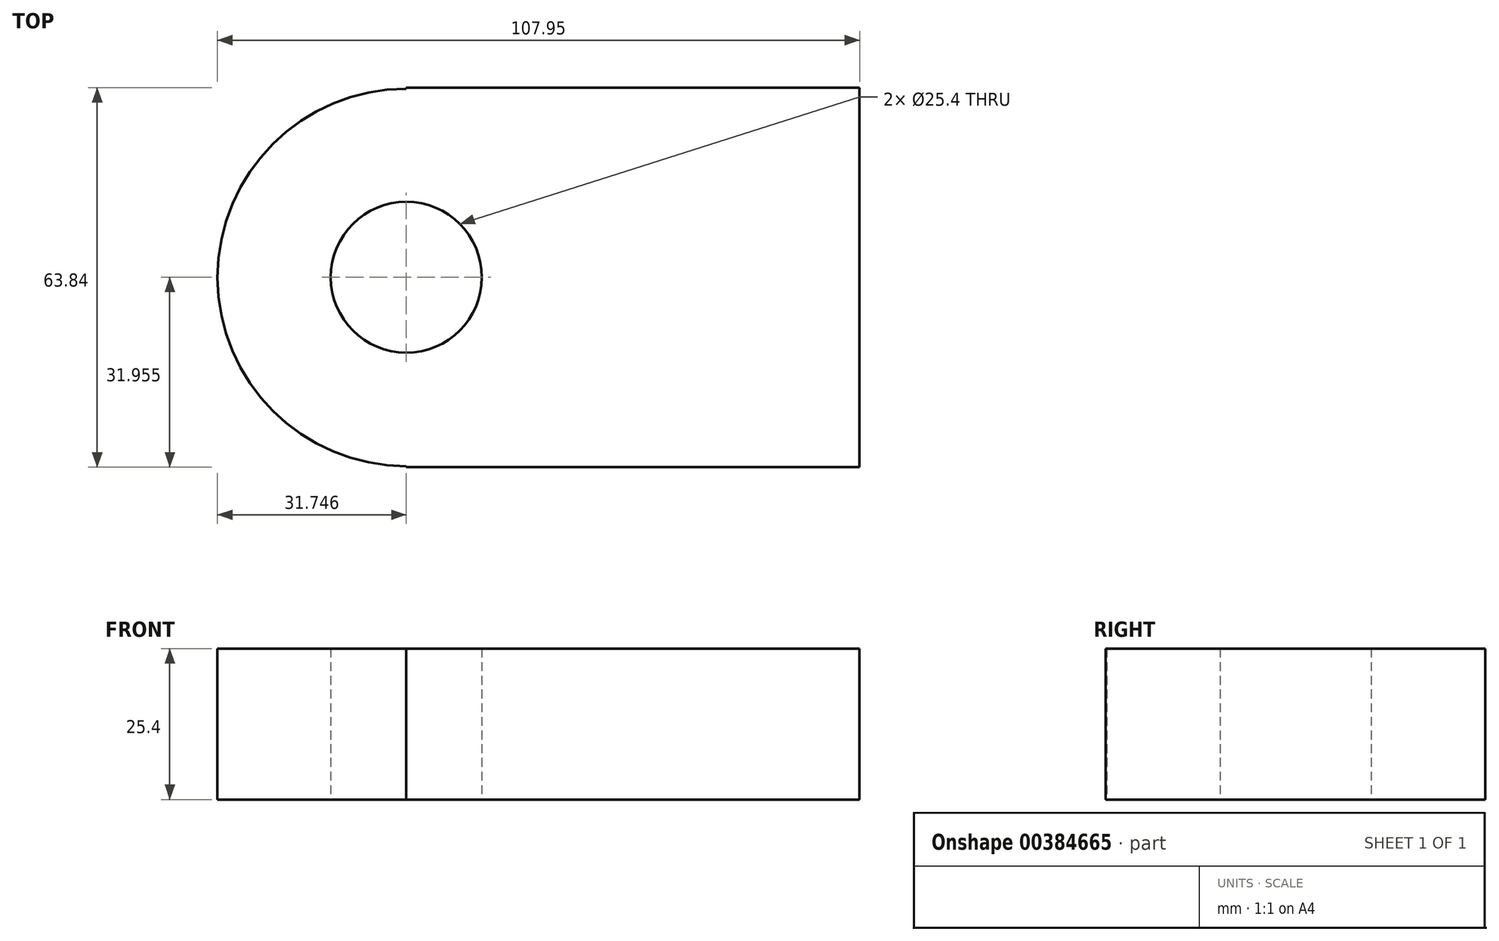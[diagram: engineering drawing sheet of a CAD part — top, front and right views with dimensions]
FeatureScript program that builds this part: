
annotation { "Feature Type Name" : "Feature", "Feature Type Description" : "" }
export const myFeature = defineFeature(function(context is Context, id is Id, definition is map)
    precondition{}
    {
        {
            var Q0;
            Q0=qCreatedBy(makeId("Top.planeOp"),FACE);
            var sketch = newSketch(context, id + "F0", { "sketchPlane" : qUnion([Q0])});
            skLineSegment(sketch, "E0.bottom", {"start": v(-38.22, -21.65) * mm, "end": v(37.98, -21.65) * mm});
            skLineSegment(sketch, "E0.top", {"start": v(-38.22, 42.2) * mm, "end": v(37.98, 42.2) * mm});
            skLineSegment(sketch, "E0.left", {"start": v(-38.22, 42.2) * mm, "end": v(-38.22, -21.65) * mm});
            skLineSegment(sketch, "E0.right", {"start": v(37.98, 42.2) * mm, "end": v(37.98, -21.65) * mm});
            skCircle(sketch, "E1", {"center": v(-38.22, 10.27) * mm, "radius": 31.75 * mm});
            skCircle(sketch, "E2", {"center": v(-38.22, 10.3) * mm, "radius": 12.7 * mm});
            skSolve(sketch);
        }
        {
            var Q0;
            {var subQ4=sQuery(id+"F0.wireOp",EDGE,"E0.bottom");Q0=makeQuery(id+"F0.imprint","IMPRINT",FACE,{"disambiguationData":[TD([[makeQuery(id+"F0.imprint","IMPRINT",EDGE,{"derivedFrom":subQ4}),1.0]])]});}
            var Q1;
            {var subQ0=sQuery(id+"F0.wireOp",EDGE,"E1");var subQ1=sQuery(id+"F0.wireOp",EDGE,"E0.left");var subQ2=makeQuery(id+"F0.imprint","INTERSECT",VERTEX,{"disambiguationData":[OD(0.0)],"derivedFrom":[subQ1,subQ0]});Q1=makeQuery(id+"F0.imprint","IMPRINT",FACE,{"disambiguationData":[TD([[makeQuery(id+"F0.imprint","IMPRINT",EDGE,{"disambiguationData":[TD([[subQ2,-1.0]])],"derivedFrom":subQ1}),1.0]])]});}
            var Q2;
            {var subQ0=sQuery(id+"F0.wireOp",EDGE,"E1");var subQ1=sQuery(id+"F0.wireOp",EDGE,"E0.left");var subQ2=makeQuery(id+"F0.imprint","INTERSECT",VERTEX,{"disambiguationData":[OD(0.0)],"derivedFrom":[subQ1,subQ0]});Q2=makeQuery(id+"F0.imprint","IMPRINT",FACE,{"disambiguationData":[TD([[makeQuery(id+"F0.imprint","IMPRINT",EDGE,{"disambiguationData":[TD([[subQ2,-1.0]])],"derivedFrom":subQ1}),-1.0]])]});}
            extrude(context, id + "F1", {"entities" : qUnion([Q0, Q1, Q2]), "depth" : 25.4 * mm});
        }
    });
